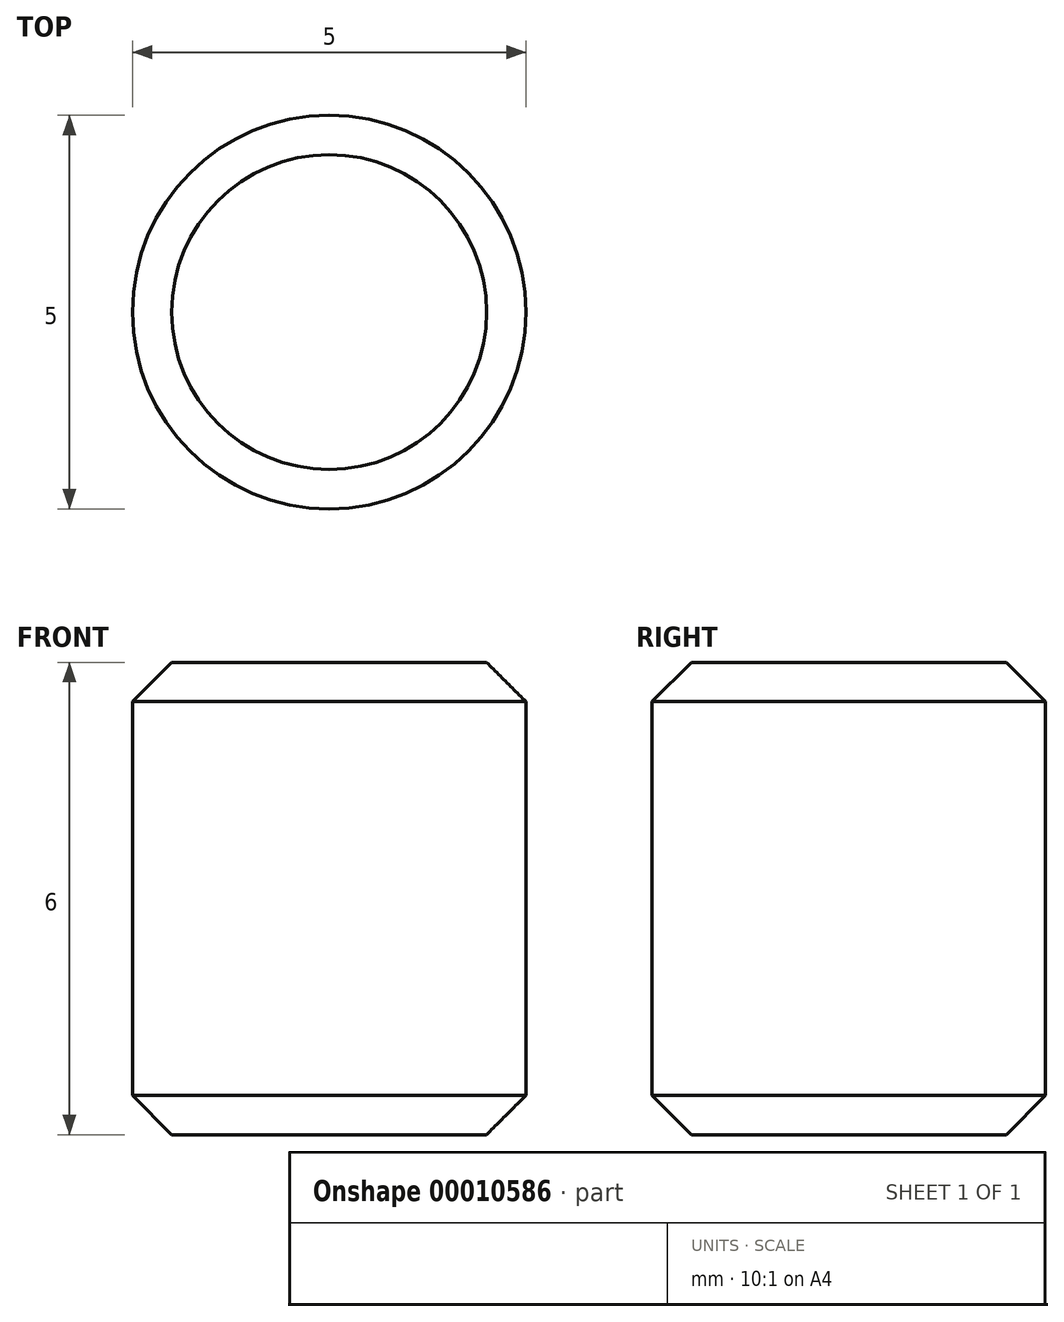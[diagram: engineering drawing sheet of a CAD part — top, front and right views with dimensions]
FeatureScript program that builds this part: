
annotation { "Feature Type Name" : "Feature", "Feature Type Description" : "" }
export const myFeature = defineFeature(function(context is Context, id is Id, definition is map)
    precondition{}
    {
        {
            var Q0;
            Q0=qCreatedBy(makeId("Top.planeOp"),FACE);
            var sketch = newSketch(context, id + "F0", { "sketchPlane" : qUnion([Q0])});
            skCircle(sketch, "E0", {"center": v(0, 0) * mm, "radius": 2.5 * mm});
            skSolve(sketch);
        }
        {
            var Q0;
            Q0=makeQuery(id+"F0.imprint","IMPRINT",FACE,{"disambiguationData":[TD([[makeQuery(id+"F0.imprint","IMPRINT",EDGE,{"derivedFrom":sQuery(id+"F0.wireOp",EDGE,"E0")}),1.0]])]});
            extrude(context, id + "F1", {"entities" : qUnion([Q0]), "depth" : 6 * mm});
        }
        {
            var Q0;
            Q0=makeQuery(id+"F1.opExtrude","CAP_EDGE",EDGE,{"disambiguationData":[OSD([sQuery(id+"F0.wireOp",EDGE,"E0")])],"isStart":false});
            var Q1;
            Q1=makeQuery(id+"F1.opExtrude","CAP_EDGE",EDGE,{"disambiguationData":[OSD([sQuery(id+"F0.wireOp",EDGE,"E0")])],"isStart":true});
            chamfer(context, id + "F2", {"entities" : qUnion([Q0, Q1]), "width" : .5 * mm, "tangentPropagation" : true});
        }
    });
